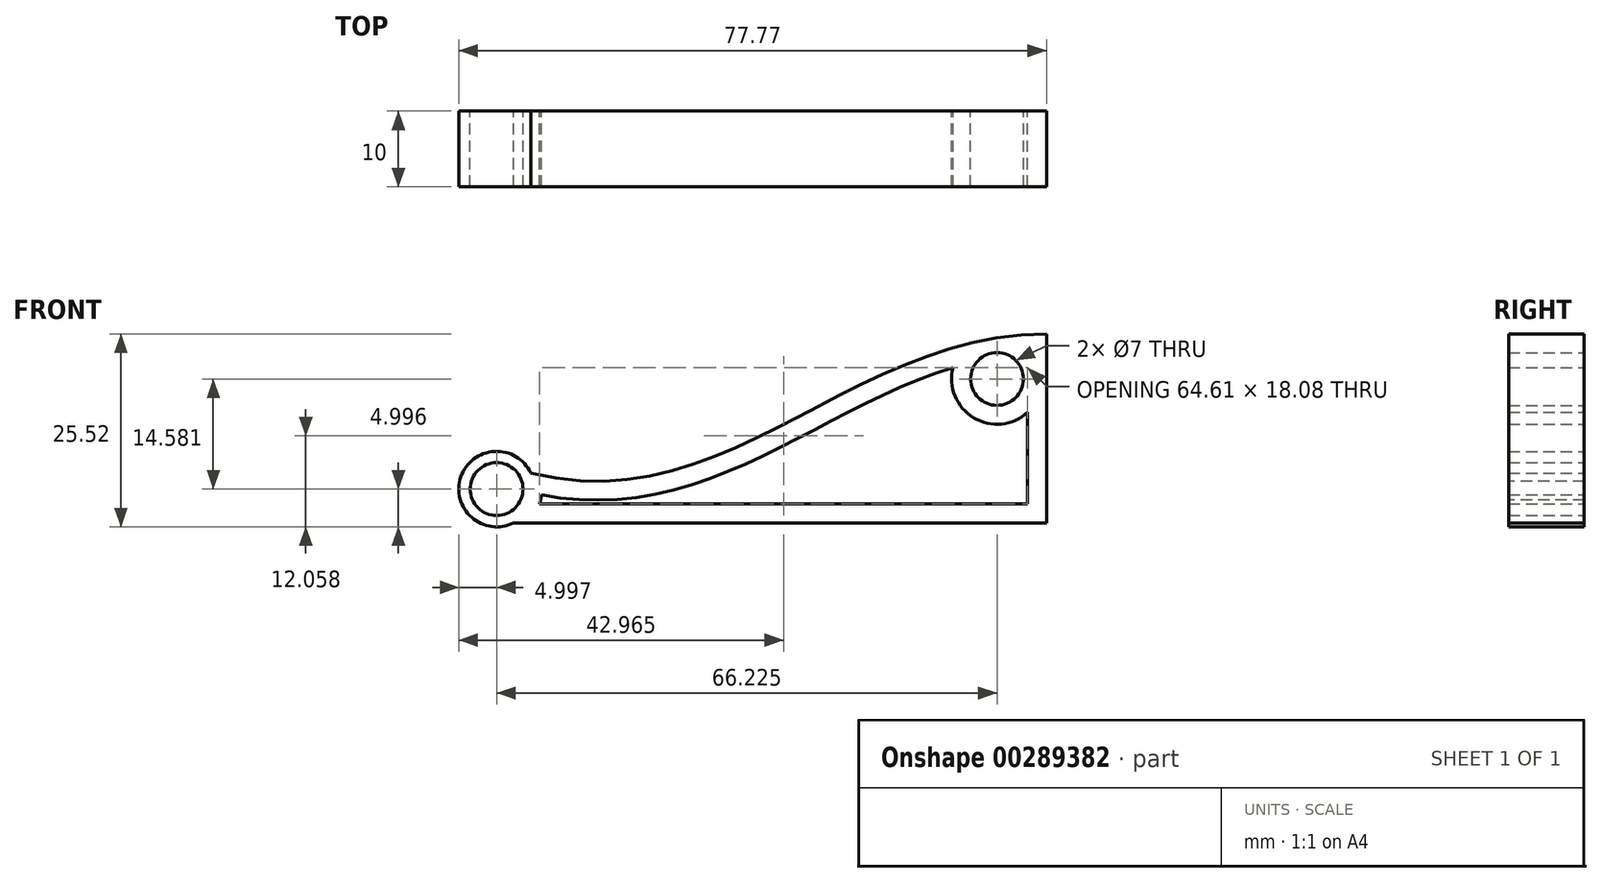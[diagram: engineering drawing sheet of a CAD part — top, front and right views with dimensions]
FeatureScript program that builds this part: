
annotation { "Feature Type Name" : "Feature", "Feature Type Description" : "" }
export const myFeature = defineFeature(function(context is Context, id is Id, definition is map)
    precondition{}
    {
        {
            var Q0;
            Q0=qCreatedBy(makeId("Front.planeOp"),FACE);
            var sketch = newSketch(context, id + "F0", { "sketchPlane" : qUnion([Q0])});
            skLineSegment(sketch, "E0", {"start": v(-19.44, -25) * mm, "end": v(55.56, -25) * mm});
            skLineSegment(sketch, "E1", {"start": v(55.56, -25) * mm, "end": v(55.56, 0) * mm});
            skCircle(sketch, "E2", {"center": v(-17.21, -20.52) * mm, "radius": 5 * mm});
            skPoint(sketch, "E2.third.point", {"position": v(-20.5, -24.29) * mm});
            skCircle(sketch, "E3", {"center": v(-17.21, -20.52) * mm, "radius": 3.5 * mm});
            skCircle(sketch, "E4", {"center": v(49.01, -5.94) * mm, "radius": 3.5 * mm});
            skFitSpline(sketch, "E5", {"points": [v(-12.7, -18.39) * mm, v(55.56, 0) * mm], "startDerivative": vector(78.03, -19.84) * mm, "endDerivative": vector(78.75, 0) * mm});
            skSolve(sketch);
        }
        {
            var Q0;
            Q0 = qSketchRegion(id + "F0", true);
            extrude(context, id + "F1", {"entities" : qUnion([Q0]), "depth" : 10 * mm});
        }
        {
            var Q0;
            Q0=makeQuery(id+"F1.opExtrude","CAP_FACE",FACE,{"disambiguationData":[OSD([sQuery(id+"F0.wireOp",EDGE,"E0"),sQuery(id+"F0.wireOp",EDGE,"E1"),sQuery(id+"F0.wireOp",EDGE,"E2"),sQuery(id+"F0.wireOp",EDGE,"E3"),sQuery(id+"F0.wireOp",EDGE,"E4"),sQuery(id+"F0.wireOp",EDGE,"E5")])],"isStart":false});
            var Q1;
            Q1=makeQuery(id+"F1.opExtrude","CAP_FACE",FACE,{"disambiguationData":[OSD([sQuery(id+"F0.wireOp",EDGE,"E0"),sQuery(id+"F0.wireOp",EDGE,"E1"),sQuery(id+"F0.wireOp",EDGE,"E2"),sQuery(id+"F0.wireOp",EDGE,"E3"),sQuery(id+"F0.wireOp",EDGE,"E4"),sQuery(id+"F0.wireOp",EDGE,"E5")])],"isStart":true});
            shell(context, id + "F2", {"entities" : qUnion([Q0, Q1]), "thickness" : 2.5 * mm});
        }
    });
